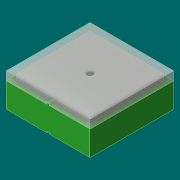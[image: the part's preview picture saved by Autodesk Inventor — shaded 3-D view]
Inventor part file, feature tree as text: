
AUTODESK INVENTOR PART (.ipt)
format: ipt  version: 2016 (Build 200138000, 138)  size: 204,800 bytes
history: native  units: mm
features: sketch x11, projected_geometry x11, extrude x8, hole x2
ambient origin geometry x8: Origin, YZ Plane, XZ Plane, XY Plane, X Axis, Y Axis, Z Axis, Center Point
bodies: Solid1 (feature_tree), Solid2 (feature_tree), Solid3 (feature_tree), Solid4 (feature_tree)
feature tree (32):
  extrude  "Extrusion1"  Depth=3.4mm
  extrude  "Extrusion2"  Depth=3.0mm
  extrude  "Extrusion6"  Depth=0.25mm TaperAngle=0.0deg
  extrude  "Extrusion3"  Depth=0.35mm TaperAngle=0.0deg
  sketch  "Sketch9"  dims[d31=0.7mm d32=0.7mm]
  extrude  "Extrusion7"  Depth=0.1mm
  hole  "Hole1"  [1 undecoded]
  extrude  "Extrusion4"  Depth=0.7mm
  hole  "Hole2"  [1 undecoded]
  extrude  "Extrusion5"  Depth=0.1mm
  extrude  "Extrusion8"  Depth=0.05mm TaperAngle=0.0deg
  sketch  "Sketch1"  dims[d0=3.4mm d1=3.4mm]
  sketch  "Sketch2"  dims[d2=1.0mm d3=0.0mm d4=3.0mm]
  sketch  "Sketch3"  dims[d5=3.0mm d6=0.25mm d7=0.0mm]
  projected_geometry  "Projected Loop1"
  projected_geometry  "Projected Loop2"
  sketch  "Sketch4"  dims[d8=0.35mm d9=0.0mm d10=0.35mm d11=0.0mm]
  projected_geometry  "Projected Loop3"
  sketch  "Sketch5"  dims[d12=0.254mm d13=6.0mm d14=4.0mm d15=2.0mm d16=90.0deg d17=0.1mm d18=20.594885mm d19=2.2mm]
  sketch  "Sketch6"  dims[d20=2.2mm]
  sketch  "Sketch7"  dims[d21=0.8mm d22=6.0mm d23=4.0mm d24=2.0mm d25=90.0deg d26=0.05mm d27=0.0mm d28=0.7mm]
  projected_geometry  "Projected Loop4"
  projected_geometry  "Projected Loop5"
  projected_geometry  "Projected Loop6"
  projected_geometry  "Projected Loop7"
  projected_geometry  "Projected Loop8"
  sketch  "Sketch8"  dims[d29=0.7mm d30=0.7mm]
  projected_geometry  "Projected Loop9"
  sketch  "Sketch10"  dims[d33=0.05mm d34=0.0mm d35=0.1mm]
  projected_geometry  "Projected Loop10"
  sketch  "Sketch11"  dims[d36=0.05mm d37=0.05mm d38=0.0mm d39=0.05mm d40=0.0mm d41=0.1mm d42=0.2mm d43=0.05mm d44=0.05mm d45=0.0mm]
  projected_geometry  "Projected Loop11"
note: 2 required parameter values undecoded (feature->parameter linkage not recoverable at this tier; creation-order binding heuristic only, values carry confidence <= 0.55)
